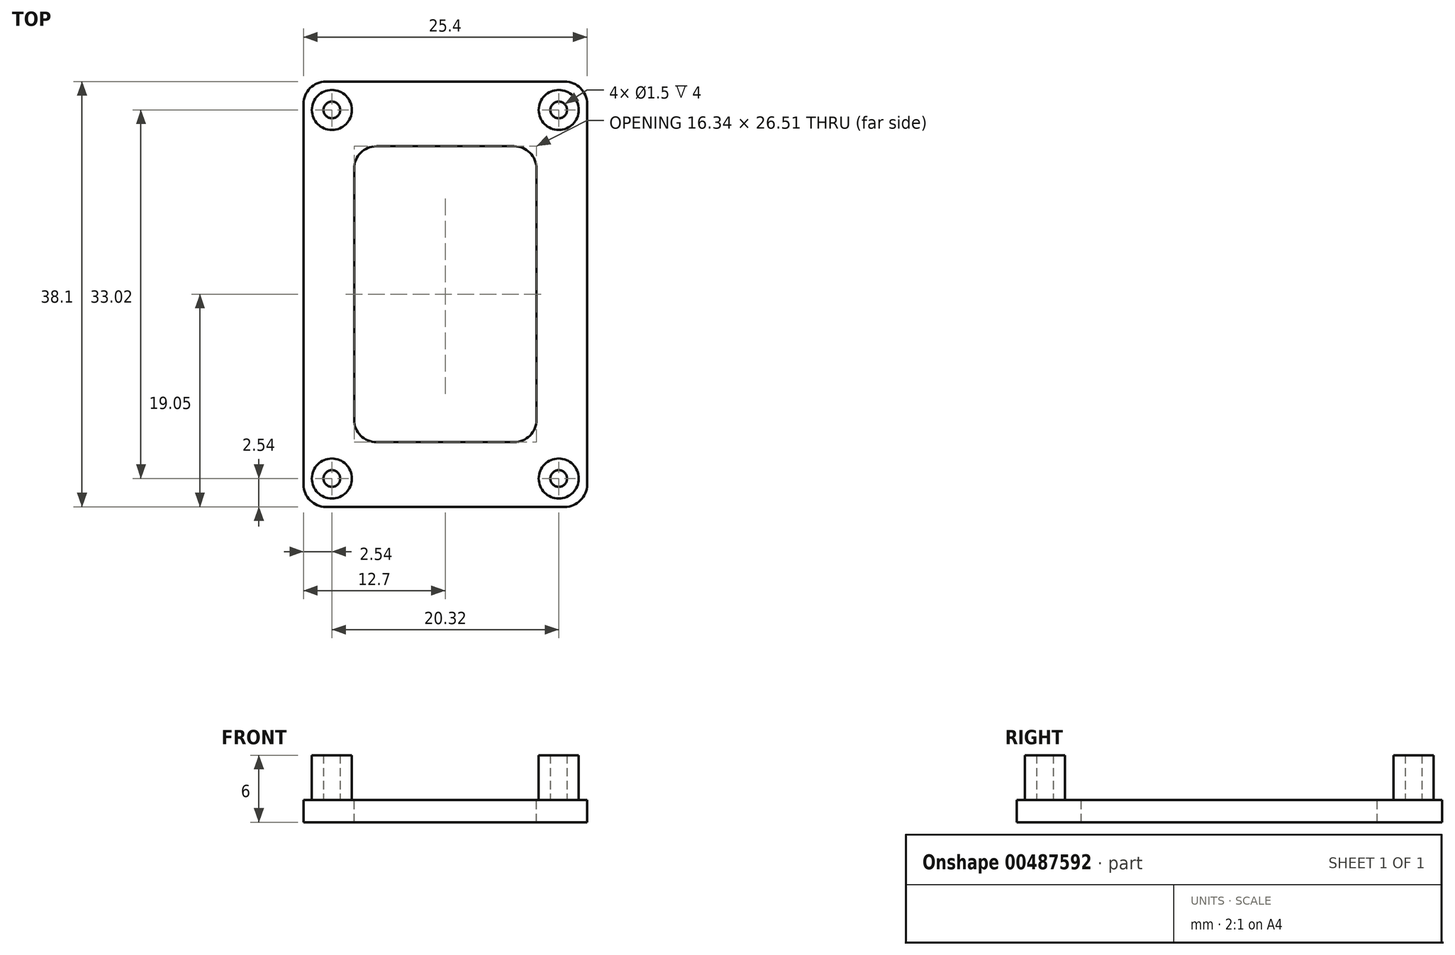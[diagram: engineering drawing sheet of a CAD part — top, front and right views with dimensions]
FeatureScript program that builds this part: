
annotation { "Feature Type Name" : "Feature", "Feature Type Description" : "" }
export const myFeature = defineFeature(function(context is Context, id is Id, definition is map)
    precondition{}
    {
        {
            var Q0;
            Q0=qCreatedBy(makeId("Top.planeOp"),FACE);
            var sketch = newSketch(context, id + "F0", { "sketchPlane" : qUnion([Q0])});
            skLineSegment(sketch, "E0.bottom", {"start": v(-10.7, 19.05) * mm, "end": v(10.7, 19.05) * mm});
            skLineSegment(sketch, "E0.top", {"start": v(-10.7, -19.05) * mm, "end": v(10.7, -19.05) * mm});
            skLineSegment(sketch, "E0.left", {"start": v(-12.7, 17.05) * mm, "end": v(-12.7, -17.05) * mm});
            skLineSegment(sketch, "E0.right", {"start": v(12.7, 17.05) * mm, "end": v(12.7, -17.05) * mm});
            skPoint(sketch, "E0.middle", {"position": v(0, 0) * mm});
            skPoint(sketch, "E1.visualSharp", {"position": v(-12.7, 19.05) * mm});
            skArc(sketch, "E1.filletArc", {"start": v(-10.7, 19.05) * mm, "mid": v(-12.11, 18.46) * mm, "end": v(-12.7, 17.05) * mm});
            skPoint(sketch, "E2.visualSharp", {"position": v(12.7, 19.05) * mm});
            skArc(sketch, "E2.filletArc", {"start": v(12.7, 17.05) * mm, "mid": v(12.11, 18.46) * mm, "end": v(10.7, 19.05) * mm});
            skPoint(sketch, "E3.visualSharp", {"position": v(12.7, -19.05) * mm});
            skArc(sketch, "E3.filletArc", {"start": v(10.7, -19.05) * mm, "mid": v(12.11, -18.46) * mm, "end": v(12.7, -17.05) * mm});
            skPoint(sketch, "E4.visualSharp", {"position": v(-12.7, -19.05) * mm});
            skArc(sketch, "E4.filletArc", {"start": v(-12.7, -17.05) * mm, "mid": v(-12.11, -18.46) * mm, "end": v(-10.7, -19.05) * mm});
            skSolve(sketch);
        }
        {
            var Q0;
            Q0 = qSketchRegion(id + "F0", true);
            extrude(context, id + "F1", {"entities" : qUnion([Q0]), "depth" : 2 * mm, "offsetDistance" : 25 * mm});
        }
        {
            var Q0;
            Q0=makeQuery(id+"F1.opExtrude","CAP_FACE",FACE,{"disambiguationData":[OSD([sQuery(id+"F0.wireOp",EDGE,"E0.bottom"),sQuery(id+"F0.wireOp",EDGE,"E0.top"),sQuery(id+"F0.wireOp",EDGE,"E0.left"),sQuery(id+"F0.wireOp",EDGE,"E0.right"),sQuery(id+"F0.wireOp",EDGE,"E1.filletArc"),sQuery(id+"F0.wireOp",EDGE,"E2.filletArc"),sQuery(id+"F0.wireOp",EDGE,"E3.filletArc"),sQuery(id+"F0.wireOp",EDGE,"E4.filletArc")])],"isStart":false});
            var sketch = newSketch(context, id + "F2", { "sketchPlane" : qUnion([Q0])});
            skCircle(sketch, "E5", {"center": v(-10.16, 16.5) * mm, "radius": 0.75 * mm});
            skCircle(sketch, "E6", {"center": v(-10.16, 16.5) * mm, "radius": 1.79 * mm});
            skCircle(sketch, "E7.MirrorC", {"center": v(10.16, 16.5) * mm, "radius": 1.79 * mm});
            skCircle(sketch, "E8.MirrorC", {"center": v(10.16, 16.5) * mm, "radius": 0.75 * mm});
            skCircle(sketch, "E9.MirrorC", {"center": v(-10.16, -16.5) * mm, "radius": 0.75 * mm});
            skCircle(sketch, "E10.MirrorC", {"center": v(10.16, -16.5) * mm, "radius": 1.79 * mm});
            skCircle(sketch, "E11.MirrorC", {"center": v(-10.16, -16.5) * mm, "radius": 1.79 * mm});
            skCircle(sketch, "E12.MirrorC", {"center": v(10.16, -16.5) * mm, "radius": 0.75 * mm});
            skSolve(sketch);
        }
        {
            var Q0;
            Q0 = qSketchRegion(id + "F2", true);
            extrude(context, id + "F3", {"entities" : qUnion([Q0]), "operationType" : NewBodyOperationType.ADD, "depth" : 4 * mm, "offsetDistance" : 25 * mm});
        }
        {
            var Q0;
            {var subQ0=sQuery(id+"F0.wireOp",EDGE,"E4.filletArc");var subQ1=sQuery(id+"F0.wireOp",EDGE,"E3.filletArc");var subQ2=sQuery(id+"F0.wireOp",EDGE,"E2.filletArc");var subQ3=sQuery(id+"F0.wireOp",EDGE,"E1.filletArc");var subQ4=sQuery(id+"F0.wireOp",EDGE,"E0.bottom");var subQ5=sQuery(id+"F0.wireOp",EDGE,"E0.right");var subQ6=sQuery(id+"F0.wireOp",EDGE,"E0.top");var subQ7=sQuery(id+"F0.wireOp",EDGE,"E0.left");Q0=makeQuery(id+"F3.boolean.opBoolean","SPLIT",FACE,{"disambiguationData":[TD([makeQuery(id+"F1.opExtrude","SWEPT_FACE",FACE,{"disambiguationData":[OSD([subQ4])]})])],"derivedFrom":makeQuery(id+"F1.opExtrude","CAP_FACE",FACE,{"disambiguationData":[OSD([subQ4,subQ6,subQ7,subQ5,subQ3,subQ2,subQ1,subQ0])],"isStart":false})});}
            var sketch = newSketch(context, id + "F4", { "sketchPlane" : qUnion([Q0])});
            skLineSegment(sketch, "E13.bottom", {"start": v(-6.17, 13.25) * mm, "end": v(6.17, 13.25) * mm});
            skLineSegment(sketch, "E13.top", {"start": v(-6.17, -13.25) * mm, "end": v(6.17, -13.25) * mm});
            skLineSegment(sketch, "E13.left", {"start": v(-8.17, 11.25) * mm, "end": v(-8.17, -11.25) * mm});
            skLineSegment(sketch, "E13.right", {"start": v(8.17, 11.25) * mm, "end": v(8.17, -11.25) * mm});
            skPoint(sketch, "E13.middle", {"position": v(0, 0) * mm});
            skPoint(sketch, "E14.visualSharp", {"position": v(-8.17, 13.25) * mm});
            skArc(sketch, "E14.filletArc", {"start": v(-6.17, 13.25) * mm, "mid": v(-7.58, 12.67) * mm, "end": v(-8.17, 11.25) * mm});
            skPoint(sketch, "E15.visualSharp", {"position": v(8.17, 13.25) * mm});
            skArc(sketch, "E15.filletArc", {"start": v(8.17, 11.25) * mm, "mid": v(7.58, 12.67) * mm, "end": v(6.17, 13.25) * mm});
            skPoint(sketch, "E16.visualSharp", {"position": v(-8.17, -13.25) * mm});
            skArc(sketch, "E16.filletArc", {"start": v(-8.17, -11.25) * mm, "mid": v(-7.58, -12.67) * mm, "end": v(-6.17, -13.25) * mm});
            skPoint(sketch, "E17.visualSharp", {"position": v(8.17, -13.25) * mm});
            skArc(sketch, "E17.filletArc", {"start": v(6.17, -13.25) * mm, "mid": v(7.58, -12.67) * mm, "end": v(8.17, -11.25) * mm});
            skSolve(sketch);
        }
        {
            var Q0;
            Q0 = qSketchRegion(id + "F4", true);
            extrude(context, id + "F5", {"entities" : qUnion([Q0]), "operationType" : NewBodyOperationType.REMOVE, "oppositeDirection" : true, "depth" : 2 * mm, "offsetDistance" : 25 * mm});
        }
    });
